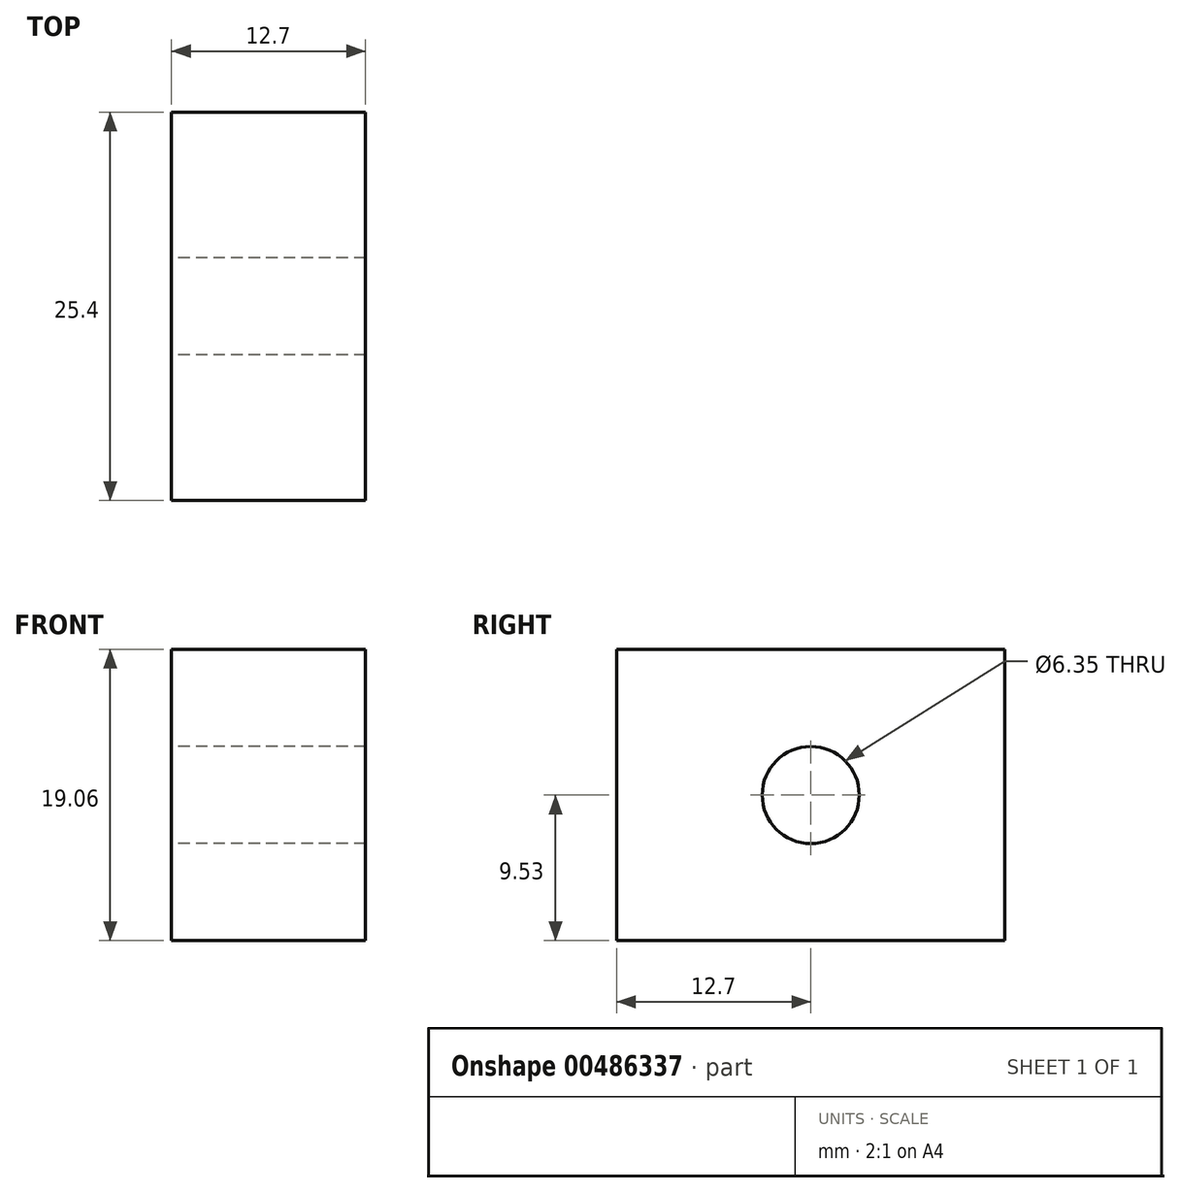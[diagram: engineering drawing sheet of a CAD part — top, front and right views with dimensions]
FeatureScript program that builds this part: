
annotation { "Feature Type Name" : "Feature", "Feature Type Description" : "" }
export const myFeature = defineFeature(function(context is Context, id is Id, definition is map)
    precondition{}
    {
        {
            var Q0;
            Q0=qCreatedBy(makeId("Right.planeOp"),FACE);
            var sketch = newSketch(context, id + "F0", { "sketchPlane" : qUnion([Q0])});
            skLineSegment(sketch, "E0.bottom", {"start": v(12.7, -9.53) * mm, "end": v(-12.7, -9.53) * mm});
            skLineSegment(sketch, "E0.top", {"start": v(12.7, 9.53) * mm, "end": v(-12.7, 9.52) * mm});
            skLineSegment(sketch, "E0.left", {"start": v(12.7, -9.53) * mm, "end": v(12.7, 9.53) * mm});
            skLineSegment(sketch, "E0.right", {"start": v(-12.7, -9.53) * mm, "end": v(-12.7, 9.52) * mm});
            skPoint(sketch, "E0.middle", {"position": v(0, 0) * mm});
            skCircle(sketch, "E1", {"center": v(0, 0) * mm, "radius": 3.18 * mm});
            skSolve(sketch);
        }
        {
            var Q0;
            Q0 = qSketchRegion(id + "F0", true);
            extrude(context, id + "F1", {"entities" : qUnion([Q0]), "depth" : 12.7 * mm});
        }
    });
